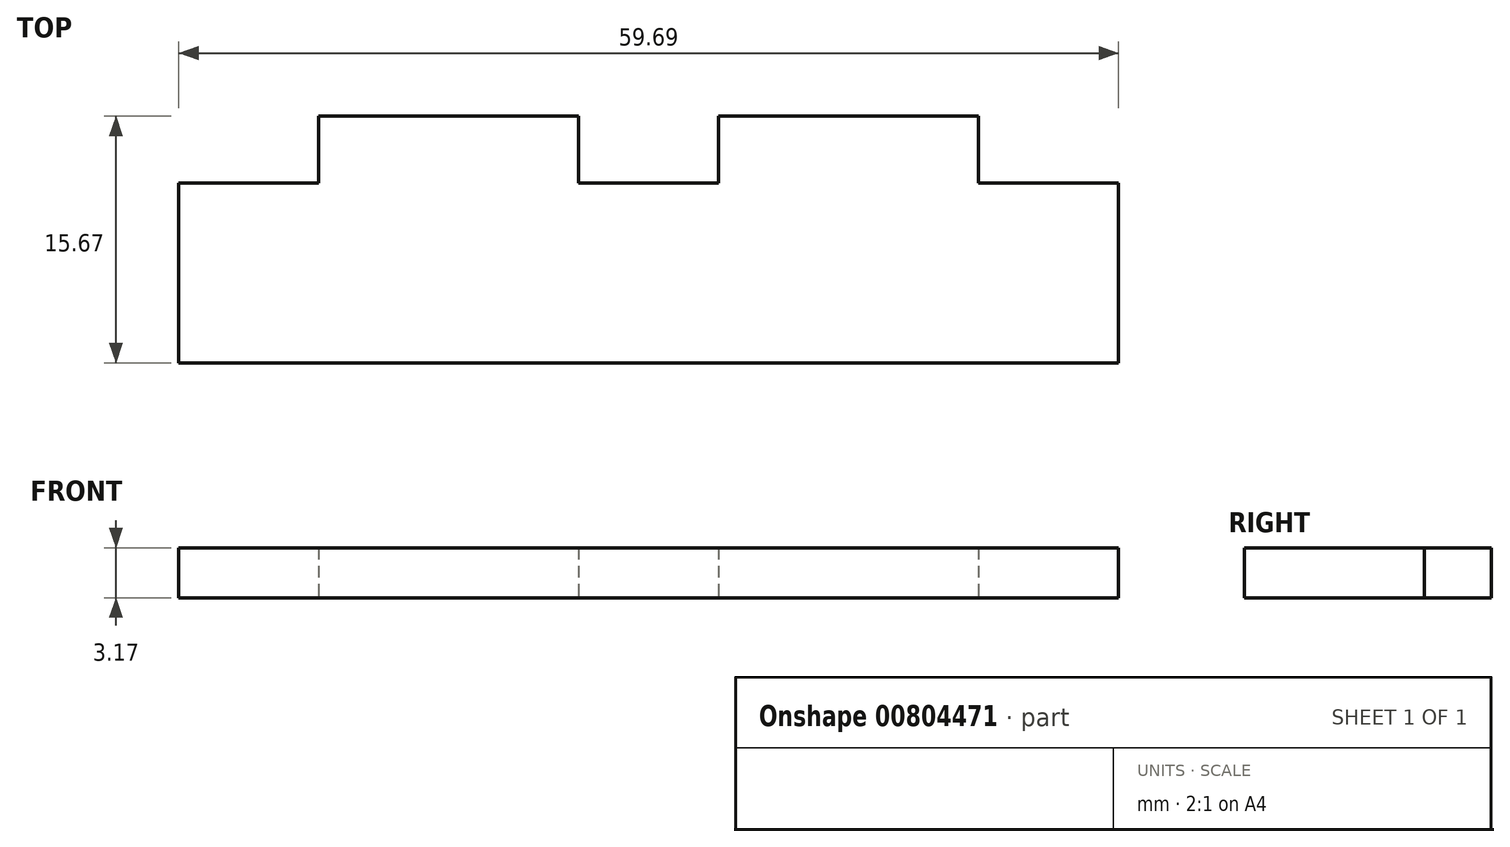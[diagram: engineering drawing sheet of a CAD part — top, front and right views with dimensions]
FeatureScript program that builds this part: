
annotation { "Feature Type Name" : "Feature", "Feature Type Description" : "" }
export const myFeature = defineFeature(function(context is Context, id is Id, definition is map)
    precondition{}
    {
        {
            var Q0;
            Q0=qCreatedBy(makeId("Top.planeOp"),FACE);
            var sketch = newSketch(context, id + "F0", { "sketchPlane" : qUnion([Q0])});
            skLineSegment(sketch, "E0.bottom", {"start": v(31.53, -5.71) * mm, "end": v(-28.16, -5.72) * mm});
            skLineSegment(sketch, "E0.left", {"start": v(31.53, -5.72) * mm, "end": v(31.53, 5.71) * mm});
            skLineSegment(sketch, "E0.right", {"start": v(-28.16, -5.72) * mm, "end": v(-28.16, 5.71) * mm});
            skPoint(sketch, "E0.middle", {"position": v(1.68, 0) * mm});
            skLineSegment(sketch, "E1", {"start": v(-28.16, 5.71) * mm, "end": v(-19.27, 5.71) * mm});
            skLineSegment(sketch, "E2", {"start": v(-19.27, 5.71) * mm, "end": v(-19.27, 9.96) * mm});
            skLineSegment(sketch, "E3", {"start": v(-19.27, 9.96) * mm, "end": v(-2.76, 9.96) * mm});
            skLineSegment(sketch, "E4", {"start": v(-2.76, 9.96) * mm, "end": v(-2.76, 5.71) * mm});
            skLineSegment(sketch, "E5", {"start": v(-2.76, 5.71) * mm, "end": v(6.13, 5.71) * mm});
            skLineSegment(sketch, "E6", {"start": v(6.13, 5.72) * mm, "end": v(6.13, 9.96) * mm});
            skLineSegment(sketch, "E7", {"start": v(6.13, 9.96) * mm, "end": v(22.64, 9.96) * mm});
            skLineSegment(sketch, "E8", {"start": v(22.64, 9.96) * mm, "end": v(22.64, 5.71) * mm});
            skLineSegment(sketch, "E9", {"start": v(22.64, 5.71) * mm, "end": v(31.53, 5.71) * mm});
            skSolve(sketch);
        }
        {
            var Q0;
            Q0=makeQuery(id+"F0.imprint","IMPRINT",FACE,{"disambiguationData":[TD([[makeQuery(id+"F0.imprint","IMPRINT",EDGE,{"derivedFrom":sQuery(id+"F0.wireOp",EDGE,"E0.bottom")}),-1.0]])]});
            extrude(context, id + "F1", {"entities" : qUnion([Q0]), "depth" : 3.17 * mm, "offsetDistance" : 25.4 * mm});
        }
    });
